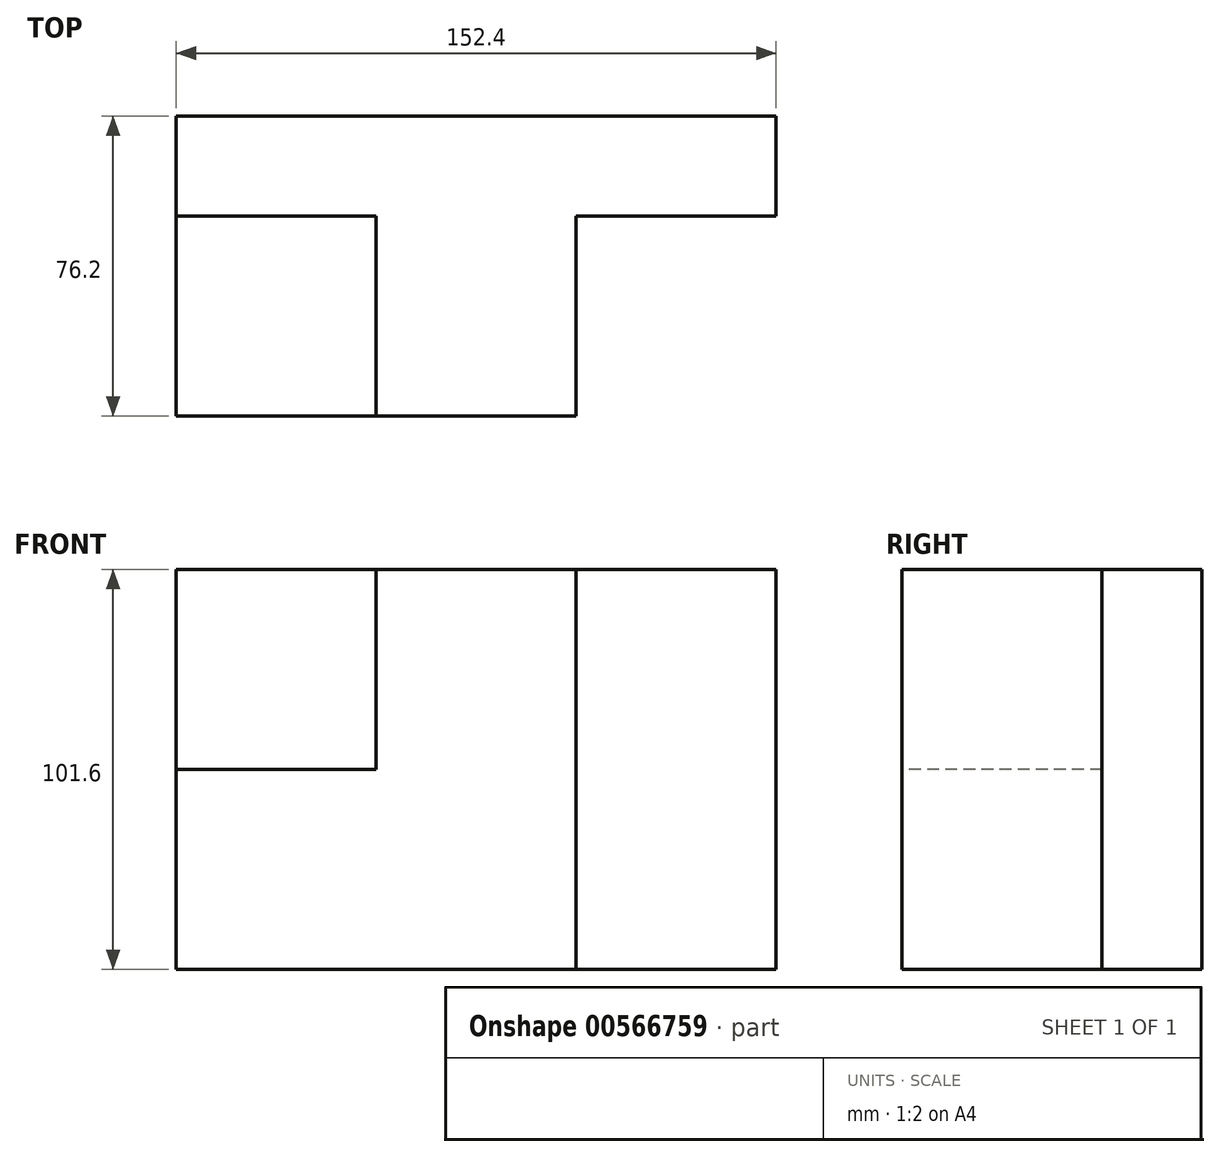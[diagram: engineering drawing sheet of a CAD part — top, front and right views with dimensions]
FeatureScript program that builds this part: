
annotation { "Feature Type Name" : "Feature", "Feature Type Description" : "" }
export const myFeature = defineFeature(function(context is Context, id is Id, definition is map)
    precondition{}
    {
        {
            var Q0;
            Q0=qCreatedBy(makeId("Top.planeOp"),FACE);
            var sketch = newSketch(context, id + "F0", { "sketchPlane" : qUnion([Q0])});
            skLineSegment(sketch, "E0.bottom", {"start": v(-60.81, 29.62) * mm, "end": v(91.59, 29.62) * mm});
            skLineSegment(sketch, "E0.top", {"start": v(-60.81, -46.58) * mm, "end": v(91.59, -46.58) * mm});
            skLineSegment(sketch, "E0.left", {"start": v(-60.81, 29.62) * mm, "end": v(-60.81, -46.58) * mm});
            skLineSegment(sketch, "E0.right", {"start": v(91.59, 29.62) * mm, "end": v(91.59, -46.58) * mm});
            skSolve(sketch);
        }
        {
            var Q0;
            Q0=makeQuery(id+"F0.imprint","IMPRINT",FACE,{"disambiguationData":[TD([[makeQuery(id+"F0.imprint","IMPRINT",EDGE,{"derivedFrom":sQuery(id+"F0.wireOp",EDGE,"E0.bottom")}),-1.0]])]});
            extrude(context, id + "F1", {"entities" : qUnion([Q0]), "depth" : 101.6 * mm, "offsetDistance" : 25.4 * mm});
        }
        {
            var Q0;
            Q0=makeQuery(id+"F1.opExtrude","SWEPT_FACE",FACE,{"disambiguationData":[OSD([sQuery(id+"F0.wireOp",EDGE,"E0.top")])]});
            var sketch = newSketch(context, id + "F2", { "sketchPlane" : qUnion([Q0])});
            skLineSegment(sketch, "E1.bottom", {"start": v(-60.81, 50.8) * mm, "end": v(-10.01, 50.8) * mm});
            skLineSegment(sketch, "E1.top", {"start": v(-60.81, 0) * mm, "end": v(-10.01, 0) * mm});
            skLineSegment(sketch, "E1.left", {"start": v(-60.81, 50.8) * mm, "end": v(-60.81, 0) * mm});
            skLineSegment(sketch, "E1.right", {"start": v(-10.01, 50.8) * mm, "end": v(-10.01, 0) * mm});
            skLineSegment(sketch, "E2.bottom", {"start": v(-10.01, 101.6) * mm, "end": v(40.79, 101.6) * mm});
            skLineSegment(sketch, "E2.top", {"start": v(-10.01, 0) * mm, "end": v(40.79, 0) * mm});
            skLineSegment(sketch, "E2.left", {"start": v(-10.01, 101.6) * mm, "end": v(-10.01, 0) * mm});
            skLineSegment(sketch, "E2.right", {"start": v(40.79, 101.6) * mm, "end": v(40.79, 0) * mm});
            skLineSegment(sketch, "E3.bottom", {"start": v(40.79, 50.8) * mm, "end": v(91.59, 50.8) * mm});
            skLineSegment(sketch, "E3.top", {"start": v(40.79, 0) * mm, "end": v(91.59, 0) * mm});
            skLineSegment(sketch, "E3.left", {"start": v(40.79, 50.8) * mm, "end": v(40.79, 0) * mm});
            skLineSegment(sketch, "E3.right", {"start": v(91.59, 50.8) * mm, "end": v(91.59, 0) * mm});
            skSolve(sketch);
        }
        {
            var Q0;
            {var subQ0=sQuery(id+"F2.wireOp",EDGE,"E1.bottom");Q0=makeQuery(id+"F2.imprint","IMPRINT",FACE,{"disambiguationData":[TD([[makeQuery(id+"F2.imprint","IMPRINT",EDGE,{"derivedFrom":subQ0}),1.0]])]});}
            extrude(context, id + "F3", {"entities" : qUnion([Q0]), "operationType" : NewBodyOperationType.REMOVE, "oppositeDirection" : true, "depth" : 50.8 * mm, "offsetDistance" : 25.4 * mm});
        }
        {
            var Q0;
            {var subQ0=sQuery(id+"F2.wireOp",EDGE,"E2.right");Q0=makeQuery(id+"F2.imprint","IMPRINT",FACE,{"disambiguationData":[TD([[makeQuery(id+"F2.imprint","IMPRINT",EDGE,{"derivedFrom":subQ0}),1.0]])]});}
            extrude(context, id + "F4", {"entities" : qUnion([Q0]), "operationType" : NewBodyOperationType.REMOVE, "oppositeDirection" : true, "depth" : 50.8 * mm, "offsetDistance" : 25.4 * mm});
        }
    });
